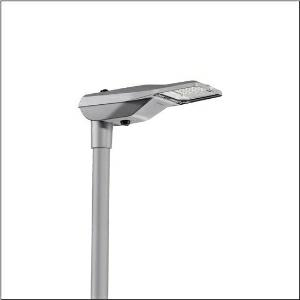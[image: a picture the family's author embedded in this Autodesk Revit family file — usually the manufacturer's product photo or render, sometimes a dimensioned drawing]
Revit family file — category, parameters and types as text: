
# Revit family: streetlight_sl_21_iq_micro___st1_0ab_5xe1m31y08cb_a08b
name_source: partatom
category: Lighting Fixtures
units: mm (PartAtom-declared; Revit-internal decimal feet)

## family parameters
Cut with Voids When Loaded = No
Host = Face
Light Source = No
Part Type = Normal
Room Calculation Point = No
Round Connector Dimension = Use Diameter
Shared = No

## types (1)
- --- (1 x LED, 2530 lm, 19.1 W, 3000K)
    Apparent Load = 19 VA
    CIE Flux Codes = 38 73 97 100 100
    Color Rendering = 70
    Color Temperature = 3000K
    Default Elevation = 1800 mm
    Description = Streetlight SL 21 iQ micro, mast luminaire, primary light control with lens, of PMMA, primary optical cover: cover, of toughened safety glass, transparent, light distribution: ST1.0aB, light emission: direct distribution, primary light characteristic: asymmetric, installation type: post-top, side-entry, LED, High Power LED, rated luminous flux: 2.530lm, luminous efficacy: 133lm/W, light colour: 730, colour temperature: 3000K, control gear: iQ-Street Remote, D4i with power reduction, control: pre-setting: logarithmic dimming characteristic, Street-Remote, Auto-Match, Temp-Guard, Lumen-Switch, Night-Set, Smart-Wire, Light-Fading, Desk-Remote (wireless, voltage-free reading and setting of iQ features in the workshop via application-optimized NFC function/RFID function), optimised constant luminous flux control (CLO 2.0), mains connection: 220..240V, AC, 50/60Hz, start of lifetime: 19W, end of service life: 20W, reduction: 9W, luminaire housing, of diecast aluminium, powder-coated, Siteco® metallic grey (DB 702S), corrosivity category C5 mid according to DIN EN ISO 12944, please order mast flange separately, inclination adjustable: 0°, 5°, 10°, 15°, sealing non-destructively replaceable, multi-level sealing system, length: 528mm, width: 235mm, height: 110mm, mast flange for spigot size: 42mm (side-entry): 5XC10008XM4, 60/48mm (side-entry/post-top): 5XC10108XM2, 76/60mm (side-entry/post-top): 5XC10108XM1, mounting height: 4..8m, Smart Interface below and above, protection rating (complete): IP66, insulation class (complete): insulation class II (safety insulation), certification: CE, ENEC, ENEC+, VDE, impact resistance: IK10, permissible operating ambient temperature for outdoor applications: -40..+50°C, standard-compliant lighting for roads and squares, packaging unit: 1 piece

Light Distribution: ST1.0aB
    Height = 110 mm
    Lamp = 1 x LED
    Lamp Light Flux = 2530 lm
    Lamp Power = 19.1 W
    Lamp count = 1
    Length = 528 mm
    Luminous efficacy = 132 lm/W
    Manufacturer = Siteco
    ModVariant = No
    Model = 5XE1M31Y08CB
    Number of Poles = 1
    OnlyDefault = Yes
    Power Factor = 1
    Product Name = Streetlight SL 21 iQ micro | ST1.0aB
    Product group = mast luminaire | pylon top
    ProductGroupID = 6100
    Protection Class = Protection class II
    Protection Degree = IP 66
    RLX_Detail_Level = 1
    RLX_Emergency_Light_Flux = 0 lm
    RLX_Emergency_Type = 0
    RLX_Emergency_Type_DB = No
    RlxData = <blob elided: 98501 chars, md5=bcf4d654>
    Socket = socket
    Standby Power = 0 W
    System Light Flux = 2530 lm
    System Power = 19 W
    Type Comments = factory setting: luminous flux: 100 % | dim-lin: 254 | 387 mA
    Type Image = l_1007239.jpg
    URL = http://relux.com
    VarID = @adj_134149
    Voltage = 0 V
    Weight = 0.00 kg
    Width = 235 mm

## geometry (parser evidence)
native form markers: Blend x4, Sweep x9
no freeform markers — native parametric forms only
